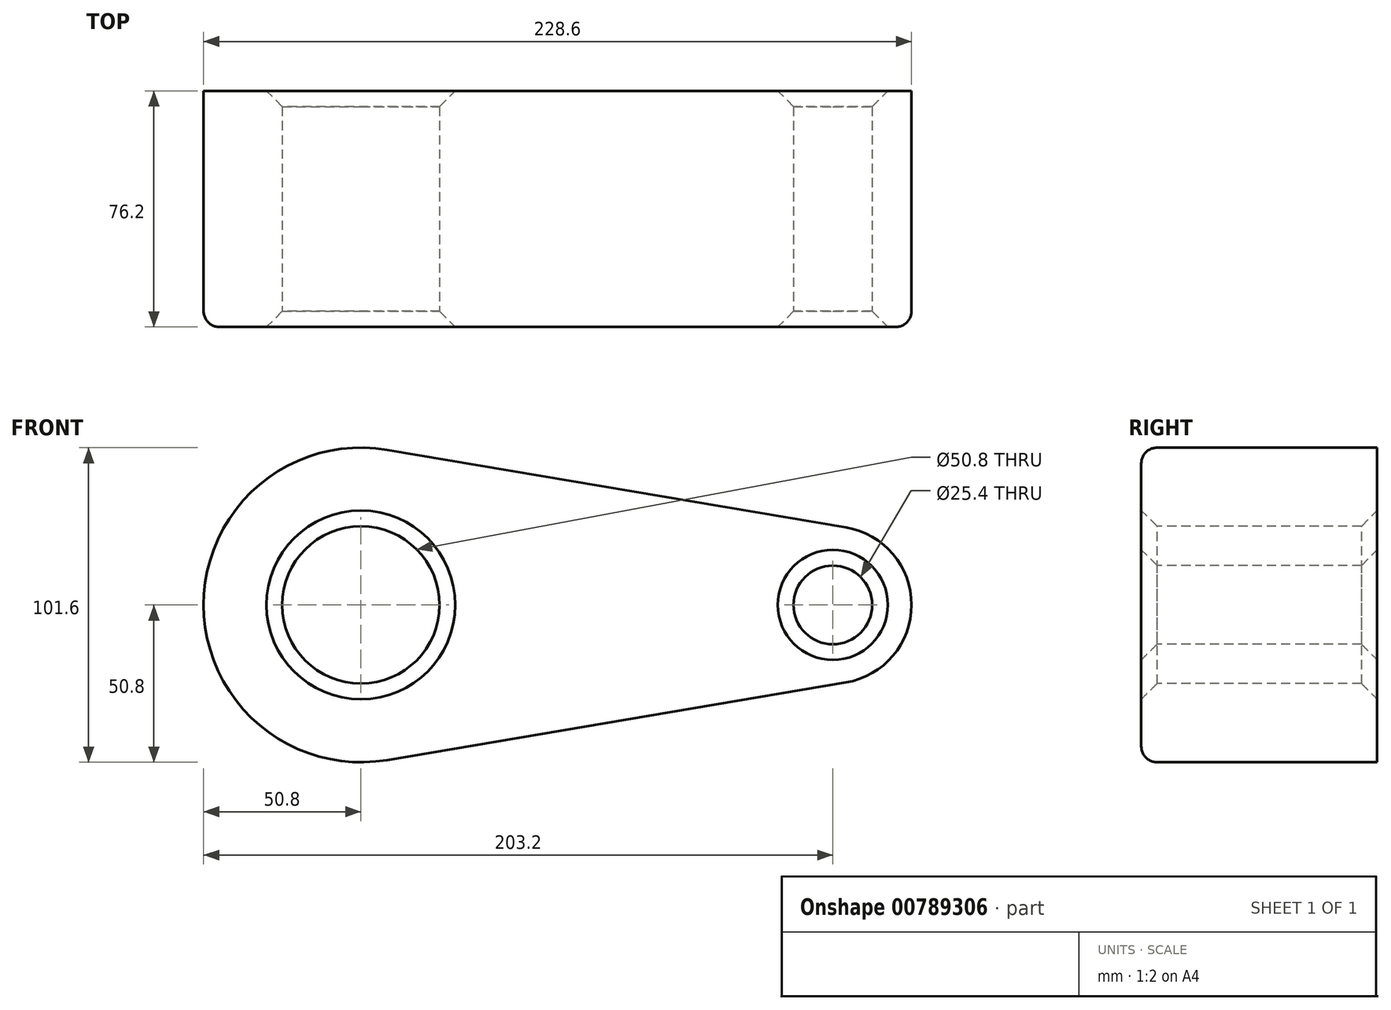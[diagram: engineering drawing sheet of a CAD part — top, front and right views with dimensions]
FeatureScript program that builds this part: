
annotation { "Feature Type Name" : "Feature", "Feature Type Description" : "" }
export const myFeature = defineFeature(function(context is Context, id is Id, definition is map)
    precondition{}
    {
        {
            var Q0;
            Q0=qCreatedBy(makeId("Front.planeOp"),FACE);
            var sketch = newSketch(context, id + "F0", { "sketchPlane" : qUnion([Q0])});
            skCircle(sketch, "E0", {"center": v(0, 0) * mm, "radius": 50.8 * mm});
            skCircle(sketch, "E1", {"center": v(152.4, 0) * mm, "radius": 25.4 * mm});
            skLineSegment(sketch, "E2", {"start": v(8.47, 50.09) * mm, "end": v(156.63, 25.04) * mm});
            skLineSegment(sketch, "E3", {"start": v(8.47, -50.09) * mm, "end": v(156.63, -25.04) * mm});
            skCircle(sketch, "E4", {"center": v(0, 0) * mm, "radius": 25.4 * mm});
            skCircle(sketch, "E5", {"center": v(152.4, 0) * mm, "radius": 12.7 * mm});
            skSolve(sketch);
        }
        {
            var Q0;
            Q0 = qSketchRegion(id + "F0", true);
            extrude(context, id + "F1", {"entities" : qUnion([Q0]), "oppositeDirection" : true, "depth" : 76.2 * mm, "offsetDistance" : 25.4 * mm});
        }
        {
            var Q0;
            Q0=makeQuery(id+"F1.opExtrude","CAP_EDGE",EDGE,{"disambiguationData":[OSD([sQuery(id+"F0.wireOp",EDGE,"E4")])],"isStart":true});
            var Q1;
            Q1=makeQuery(id+"F1.opExtrude","CAP_EDGE",EDGE,{"disambiguationData":[OSD([sQuery(id+"F0.wireOp",EDGE,"E4")])],"isStart":false});
            chamfer(context, id + "F2", {"entities" : qUnion([Q0, Q1]), "width" : 5.08 * mm, "tangentPropagation" : true});
        }
        {
            var Q0;
            Q0=makeQuery(id+"F1.opExtrude","CAP_EDGE",EDGE,{"disambiguationData":[OSD([sQuery(id+"F0.wireOp",EDGE,"E5")])],"isStart":false});
            var Q1;
            Q1=makeQuery(id+"F1.opExtrude","CAP_EDGE",EDGE,{"disambiguationData":[OSD([sQuery(id+"F0.wireOp",EDGE,"E5")])],"isStart":true});
            chamfer(context, id + "F3", {"entities" : qUnion([Q0, Q1]), "width" : 5.08 * mm, "tangentPropagation" : true});
        }
        {
            var Q0;
            Q0=makeQuery(id+"F1.opExtrude","CAP_EDGE",EDGE,{"disambiguationData":[OSD([sQuery(id+"F0.wireOp",EDGE,"E3")])],"isStart":true});
            fillet(context, id + "F4", {"entities" : qUnion([Q0]), "radius" : 5.08 * mm, "tangentPropagation" : true, "allowEdgeOverflow" : false});
        }
    });
